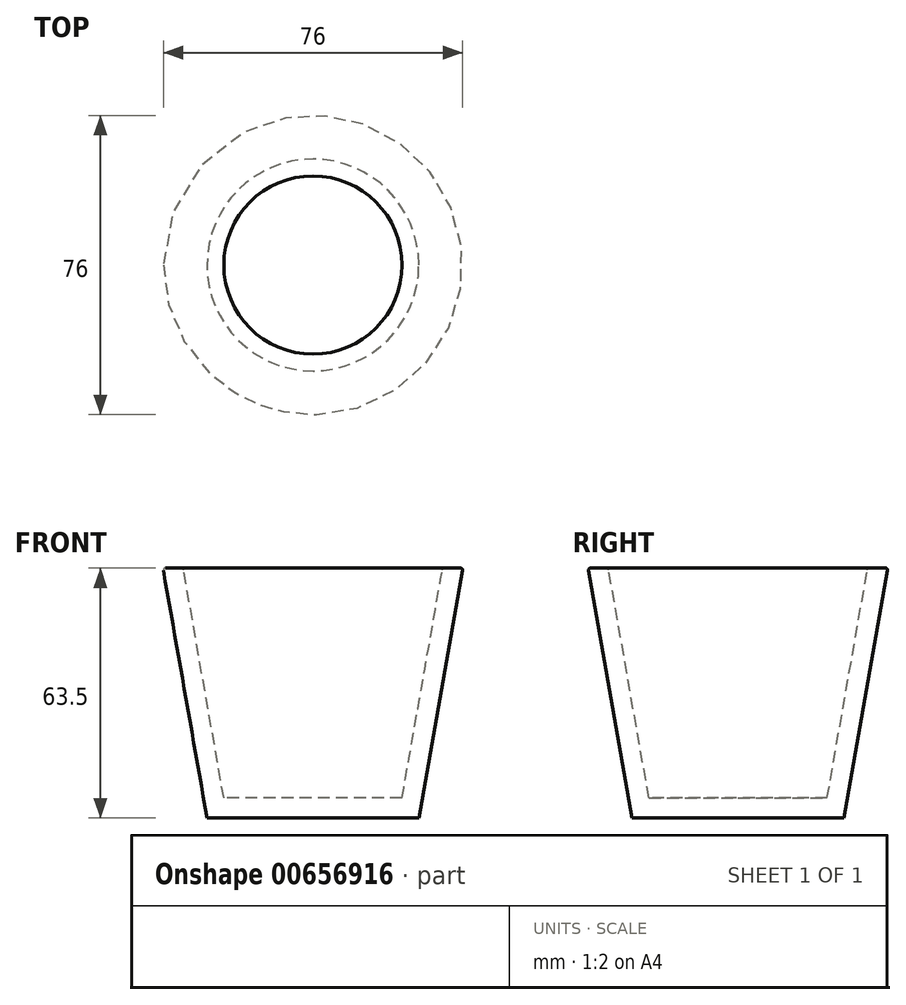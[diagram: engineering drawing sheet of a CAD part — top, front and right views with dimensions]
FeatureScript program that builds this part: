
annotation { "Feature Type Name" : "Feature", "Feature Type Description" : "" }
export const myFeature = defineFeature(function(context is Context, id is Id, definition is map)
    precondition{}
    {
        {
            var Q0;
            Q0=qCreatedBy(makeId("Front.planeOp"),FACE);
            var sketch = newSketch(context, id + "F0", { "sketchPlane" : qUnion([Q0])});
            skLineSegment(sketch, "E0", {"start": v(0, 63.5) * mm, "end": v(-38.1, 63.5) * mm});
            skLineSegment(sketch, "E1", {"start": v(-38.1, 63.5) * mm, "end": v(-26.9, 0) * mm});
            skLineSegment(sketch, "E2", {"start": v(-26.9, 0) * mm, "end": v(0, 0) * mm});
            skLineSegment(sketch, "E3", {"start": v(0, 0) * mm, "end": v(0, 63.5) * mm});
            skSolve(sketch);
        }
        {
            var Q0;
            Q0=makeQuery(id+"F0.imprint","IMPRINT",FACE,{"disambiguationData":[TD([[makeQuery(id+"F0.imprint","IMPRINT",EDGE,{"derivedFrom":sQuery(id+"F0.wireOp",EDGE,"E0")}),1.0]])]});
            var Q1;
            Q1=sQuery(id+"F0.wireOp",EDGE,"E3");
            revolve(context, id + "F1", {"entities" : qUnion([Q0]), "axis" : qUnion([Q1]), "revolveType" : RevolveType.FULL});
        }
        {
            var Q0;
            Q0=makeQuery(id+"F1.opRevolve","SWEPT_FACE",FACE,{"disambiguationData":[OSD([sQuery(id+"F0.wireOp",EDGE,"E0")])]});
            shell(context, id + "F2", {"entities" : qUnion([Q0]), "thickness" : 5.08 * mm});
        }
        {
            var Q0;
            Q0=makeQuery(id+"F2.opShell","OFFSET_EDGE",EDGE,{"disambiguationData":[OSD([sQuery(id+"F0.wireOp",EDGE,"E0"),sQuery(id+"F0.wireOp",EDGE,"E1")])]});
            fillet(context, id + "F3", {"entities" : qUnion([Q0]), "radius" : 0.5 * mm, "tangentPropagation" : true, "allowEdgeOverflow" : false});
        }
        {
            var Q0;
            Q0=makeQuery(id+"F1.opRevolve","SWEPT_EDGE",EDGE,{"disambiguationData":[OSD([sQuery(id+"F0.wireOp",EDGE,"E0"),sQuery(id+"F0.wireOp",EDGE,"E1")])]});
            fillet(context, id + "F4", {"entities" : qUnion([Q0]), "radius" : 0.5 * mm, "tangentPropagation" : true, "allowEdgeOverflow" : false});
        }
        {
            var Q0;
            Q0=qCreatedBy(makeId("Front.planeOp"),FACE);
            var sketch = newSketch(context, id + "F5", { "sketchPlane" : qUnion([Q0])});
            skLineSegment(sketch, "E4", {"start": v(0, 64.02) * mm, "end": v(0, 51.4) * mm, "construction": true});
            skCircle(sketch, "E5", {"center": v(0, 51.4) * mm, "radius": 3.84 * mm});
            skSolve(sketch);
        }
        {
            var Q0;
            Q0=sQuery(id+"F5.wireOp",EDGE,"E5");
            var Q1;
            Q1=makeQuery(id+"F1.opRevolve","SWEPT_FACE",FACE,{"disambiguationData":[OSD([sQuery(id+"F0.wireOp",EDGE,"E1")])]});
            extrude(context, id + "F6", {"bodyType" : ToolBodyType.SURFACE, "surfaceEntities" : qUnion([Q0]), "endBound" : BoundingType.UP_TO_SURFACE, "depth" : 25.4 * mm, "endBoundEntityFace" : qUnion([Q1]), "offsetDistance" : 25.4 * mm});
        }
    });
